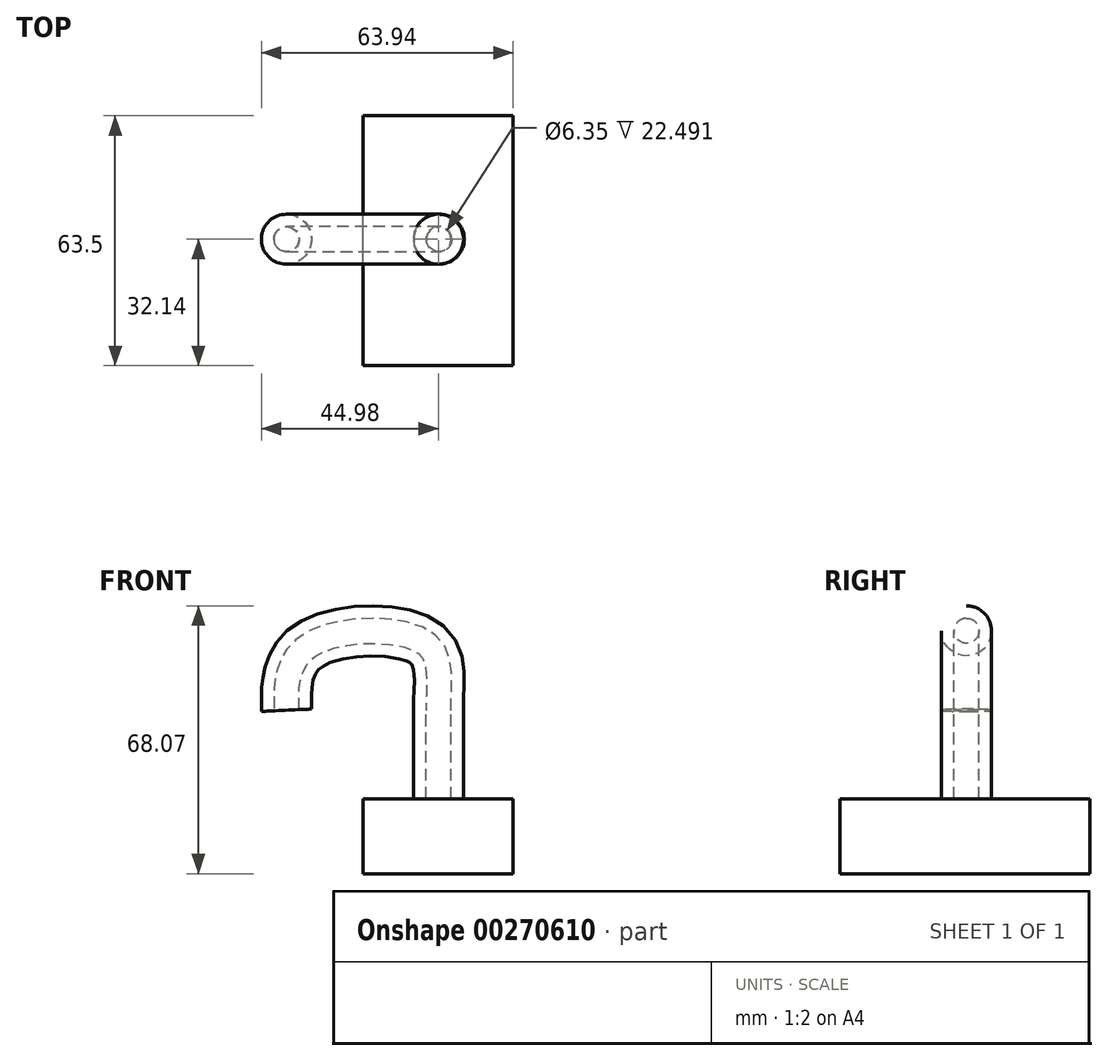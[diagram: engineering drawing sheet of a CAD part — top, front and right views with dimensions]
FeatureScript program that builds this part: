
annotation { "Feature Type Name" : "Feature", "Feature Type Description" : "" }
export const myFeature = defineFeature(function(context is Context, id is Id, definition is map)
    precondition{}
    {
        {
            var Q0;
            Q0=qCreatedBy(makeId("Top.planeOp"),FACE);
            var sketch = newSketch(context, id + "F0", { "sketchPlane" : qUnion([Q0])});
            skCircle(sketch, "E0", {"center": v(0, 0) * mm, "radius": 6.35 * mm});
            skCircle(sketch, "E1", {"center": v(0, 0) * mm, "radius": 3.18 * mm});
            skSolve(sketch);
        }
        {
            var Q0;
            Q0=qCreatedBy(makeId("Front.planeOp"),FACE);
            var sketch = newSketch(context, id + "F1", { "sketchPlane" : qUnion([Q0])});
            skLineSegment(sketch, "E2", {"start": v(0, 0) * mm, "end": v(0, 22.5) * mm});
            skFitSpline(sketch, "E3", {"points": [v(0, 22.5) * mm, v(-2.95, 39.27) * mm, v(-31.7, 39.64) * mm, v(-38.35, 29.68) * mm, v(-38.53, 22.5) * mm], "startDerivative": vector(0, 75.5) * mm, "endDerivative": vector(1.94, -39.77) * mm});
            skSolve(sketch);
        }
        {
            var Q0;
            Q0=makeQuery(id+"F0.imprint","IMPRINT",FACE,{"disambiguationData":[TD([[makeQuery(id+"F0.imprint","IMPRINT",EDGE,{"derivedFrom":sQuery(id+"F0.wireOp",EDGE,"E0")}),1.0]])]});
            var Q1;
            Q1=sQuery(id+"F1.wireOp",EDGE,"E2");
            var Q2;
            Q2=sQuery(id+"F1.wireOp",EDGE,"E3");
            sweep(context, id + "F2", {"profiles" : qUnion([Q0]), "path" : qUnion([Q1, Q2])});
        }
        {
            var Q0;
            Q0=qCreatedBy(makeId("Top.planeOp"),FACE);
            var sketch = newSketch(context, id + "F3", { "sketchPlane" : qUnion([Q0])});
            skLineSegment(sketch, "E4.bottom", {"start": v(-19.14, -32.14) * mm, "end": v(18.96, -32.14) * mm});
            skLineSegment(sketch, "E4.top", {"start": v(-19.14, 31.36) * mm, "end": v(18.96, 31.36) * mm});
            skLineSegment(sketch, "E4.left", {"start": v(-19.14, -32.14) * mm, "end": v(-19.14, 31.36) * mm});
            skLineSegment(sketch, "E4.right", {"start": v(18.96, -32.14) * mm, "end": v(18.96, 31.36) * mm});
            skSolve(sketch);
        }
        {
            var Q0;
            Q0=makeQuery(id+"F3.imprint","IMPRINT",FACE,{"disambiguationData":[TD([[makeQuery(id+"F3.imprint","IMPRINT",EDGE,{"derivedFrom":sQuery(id+"F3.wireOp",EDGE,"E4.bottom")}),1.0]])]});
            extrude(context, id + "F4", {"entities" : qUnion([Q0]), "operationType" : NewBodyOperationType.ADD, "oppositeDirection" : true, "depth" : 19.05 * mm});
        }
    });
